# Revit family: Domotics-DomesticRanges-GEWISS-CHORUS_POWER-SOCKET-OUTLET_ISR
name_source: partatom
category: Apparecchi elettrici
revit_build: Autodesk Revit 2016 (Build: 20161004_0715(x64)
units: mm (PartAtom-declared; Revit-internal decimal feet)

## family parameters
Condiviso = Sì
Host = Superficie
Mantenere orientamento annotazione = Sì
Punto di calcolo locali = Sì
Quota connettore circolare = Usa diametro
Taglio con vuoti quando caricato = Sì
Tipo di parte = Normale

## types (4) — shared parameters
Breaking capacity: = 1.25 In (100 position changes)
Carico apparente = 0 VA
Catalogue = DOMOTICS
Catalogue Range = CHORUS - DOMESTIC RANGE
Category = Socket-outlet
Characteristics = With safety shields
Description. = Socket-outlet
Electrocod = 0131
For plug pins = Round Ã˜ 4 / 4.4 mm
Glow Wire Test = 850°C
IDF = 335dd338-4dff-465e-8347-e3abaa6ba4eb
IDT = db385701-3ace-4d86-9a66-d7bb354956f2
Immagine tipo = GW14281.jpg
Insulation resistance = > 5 MOhm
N. poli = 1
No. Chorus modules = 2
No. Chorus modules: = 2
Produttore = GEWISS S.p.A.
Prolonged operation (no.of position changes) = 10.000 at In 250 V ac cosÃ˜=0,8
Prospetto di default = 1219 mm
Resistance at test voltage = 2000 V at 50 Hz for 1 minute
SEO = Socket outlet
Standard = Israeli
Standard: = Israeli
Standard; = IEC 60884-1
TXT ELETTRICO = 16
Technical sheet = https://www.gewiss.com
Terminal grip on cable traction = > 50 N
Terminal tightening capacity flexible cables (mm2) = min. 0,75 - max. 2x4
Terminal tightening capacity rigid cables (mm2) = min. 0,5 - max. 2x2,5
Thermo-pressure with ball = 125
Tipo_ = CHORUS PRESE ISRAELE_GENERICO : GW14281 Presa 2M 2P+T 16A standard israeliano titanio
URL = https://www.gewiss.com
Version file RFA = 19.0
Volt = 230 V
Voltage = 250 V ac
Voltage: = 250 V ac
Wiring terminals = With screw

## per-type parameters (varying)
| type | Colour | Description: | Descrizione | EAN code | Modello | Type | Type: |
| GW10281 - Socket outlet 2M 2P+E 16A isr white | White | 2P+E - 16 A illuminable | S. OUTLET 2M 2P+E 16A ISR WHITE | 8011564262416 | GW10281 |  |  |
| GW14281 - Socket outlet 2M 2P+E 16A israeli st titanium | Titanium | 2P+E - 16A | SOCKET 2M 2P+E 16A ISRAELI ST TITANIUM | 8011564266407 | GW14281 |  |  |
| GW10291 - Socket outlet 2M 2P+E 16A isr ded. Lines red | Red | 2P+E - 16 A illuminable | S. OUTLET 2M 2P+E 16A ISR DED. LINES RED | 8011564265004 | GW10291 | For allocated lines | For allocated lines |
| GW12281 - Socket outlet 2M 2P+E 16A israeli st black | Black | 2P+E - 16A | SOCKET 2M 2P+E 16A ISRAELI ST BLACK | 8011564266940 | GW12281 |  |  |

note: source unit labels omitted for Thermo-pressure with ball — the stored unit's dimension contradicts the parameter name (converter mislabeling)

## geometry (parser evidence)
native form markers: Sweep x2
no freeform markers — native parametric forms only
